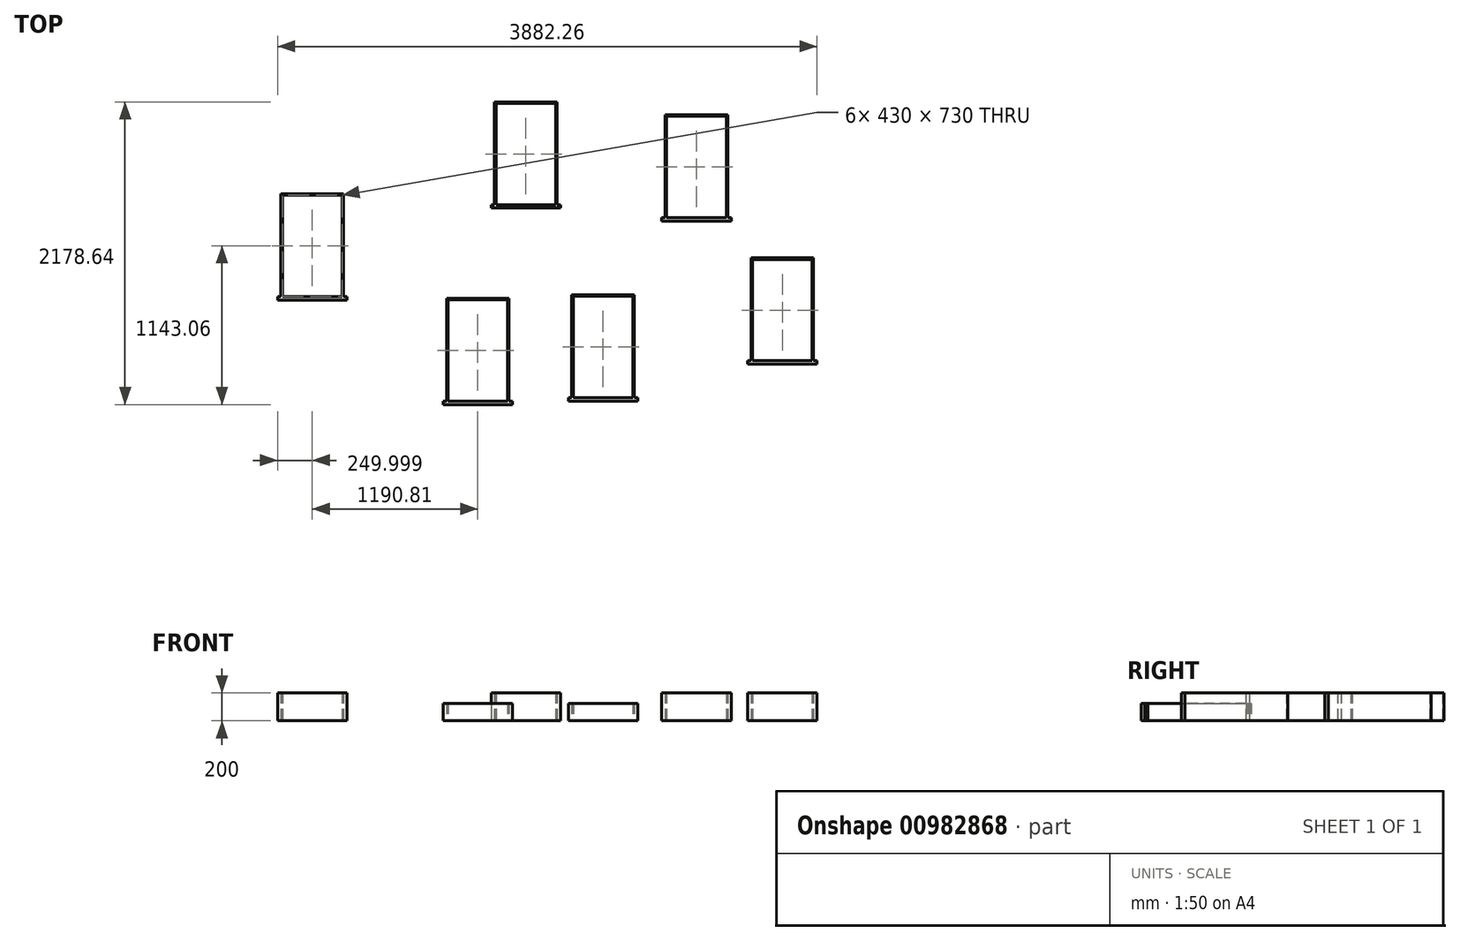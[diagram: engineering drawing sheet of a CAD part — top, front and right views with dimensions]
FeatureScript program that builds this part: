
annotation { "Feature Type Name" : "Feature", "Feature Type Description" : "" }
export const myFeature = defineFeature(function(context is Context, id is Id, definition is map)
    precondition{}
    {
        {
            var Q0;
            Q0=qCreatedBy(makeId("Top.planeOp"),FACE);
            var sketch = newSketch(context, id + "F0", { "sketchPlane" : qUnion([Q0])});
            skLineSegment(sketch, "E0.left", {"start": v(-4019.96, -780.79) * mm, "end": v(-4019.96, -1080.79) * mm});
            skLineSegment(sketch, "E1.top", {"start": v(-4044.96, -1275.79) * mm, "end": v(-4019.96, -1275.79) * mm});
            skLineSegment(sketch, "E2.left", {"start": v(-4019.96, -1275.79) * mm, "end": v(-4019.96, -1250.79) * mm});
            skLineSegment(sketch, "E3", {"start": v(-4019.96, -1250.79) * mm, "end": v(-3544.96, -1250.79) * mm});
            skLineSegment(sketch, "E4", {"start": v(-4019.96, -1275.79) * mm, "end": v(-3544.96, -1275.79) * mm});
            skLineSegment(sketch, "E5", {"start": v(-4019.96, -1250.79) * mm, "end": v(-4044.96, -1250.79) * mm});
            skLineSegment(sketch, "E6", {"start": v(-3544.96, -1275.79) * mm, "end": v(-3544.96, -1250.79) * mm});
            skLineSegment(sketch, "E7", {"start": v(-4044.96, -1275.79) * mm, "end": v(-4044.96, -1250.79) * mm});
            skLineSegment(sketch, "E8", {"start": v(-3569.96, -1271.37) * mm, "end": v(-3569.96, -510.79) * mm});
            skLineSegment(sketch, "E9", {"start": v(-4019.96, -780.79) * mm, "end": v(-4019.96, -510.79) * mm});
            skLineSegment(sketch, "E10", {"start": v(-4019.96, -1080.79) * mm, "end": v(-4019.96, -1250.79) * mm});
            skLineSegment(sketch, "E11", {"start": v(-3569.96, -510.79) * mm, "end": v(-4019.96, -510.79) * mm});
            skLineSegment(sketch, "E12", {"start": v(-4009.96, -1250.79) * mm, "end": v(-4009.96, -510.79) * mm});
            skLineSegment(sketch, "E13", {"start": v(-4019.96, -520.79) * mm, "end": v(-3569.96, -520.79) * mm});
            skLineSegment(sketch, "E14", {"start": v(-3579.96, -510.79) * mm, "end": v(-3579.96, -1250.79) * mm});
            skLineSegment(sketch, "E15", {"start": v(-3569.96, -1271.37) * mm, "end": v(-3569.96, -1275.79) * mm});
            skLineSegment(sketch, "E16.left", {"start": v(-2829.15, -1533.85) * mm, "end": v(-2829.15, -1833.85) * mm});
            skLineSegment(sketch, "E17.top", {"start": v(-2854.15, -2028.85) * mm, "end": v(-2829.15, -2028.85) * mm});
            skLineSegment(sketch, "E18.left", {"start": v(-2829.15, -2028.85) * mm, "end": v(-2829.15, -2003.85) * mm});
            skLineSegment(sketch, "E19", {"start": v(-2829.15, -2003.85) * mm, "end": v(-2354.15, -2003.85) * mm});
            skLineSegment(sketch, "E20", {"start": v(-2829.15, -2028.85) * mm, "end": v(-2354.15, -2028.85) * mm});
            skLineSegment(sketch, "E21", {"start": v(-2829.15, -2003.85) * mm, "end": v(-2854.15, -2003.85) * mm});
            skLineSegment(sketch, "E22", {"start": v(-2354.15, -2028.85) * mm, "end": v(-2354.15, -2003.85) * mm});
            skLineSegment(sketch, "E23", {"start": v(-2854.15, -2028.85) * mm, "end": v(-2854.15, -2003.85) * mm});
            skLineSegment(sketch, "E24", {"start": v(-2379.15, -2024.43) * mm, "end": v(-2379.15, -1263.85) * mm});
            skLineSegment(sketch, "E25", {"start": v(-2829.15, -1533.85) * mm, "end": v(-2829.15, -1263.85) * mm});
            skLineSegment(sketch, "E26", {"start": v(-2829.15, -1833.85) * mm, "end": v(-2829.15, -2003.85) * mm});
            skLineSegment(sketch, "E27", {"start": v(-2379.15, -1263.85) * mm, "end": v(-2829.15, -1263.85) * mm});
            skLineSegment(sketch, "E28", {"start": v(-2819.15, -2003.85) * mm, "end": v(-2819.15, -1263.85) * mm});
            skLineSegment(sketch, "E29", {"start": v(-2829.15, -1273.85) * mm, "end": v(-2379.15, -1273.85) * mm});
            skLineSegment(sketch, "E30", {"start": v(-2389.15, -1263.85) * mm, "end": v(-2389.15, -2003.85) * mm});
            skLineSegment(sketch, "E31", {"start": v(-2379.15, -2024.43) * mm, "end": v(-2379.15, -2028.85) * mm});
            skLineSegment(sketch, "E32.left", {"start": v(-1927.88, -1509.15) * mm, "end": v(-1927.88, -1809.15) * mm});
            skLineSegment(sketch, "E33.top", {"start": v(-1952.88, -2004.15) * mm, "end": v(-1927.88, -2004.15) * mm});
            skLineSegment(sketch, "E34.left", {"start": v(-1927.88, -2004.15) * mm, "end": v(-1927.88, -1979.15) * mm});
            skLineSegment(sketch, "E35", {"start": v(-1927.88, -1979.15) * mm, "end": v(-1452.88, -1979.15) * mm});
            skLineSegment(sketch, "E36", {"start": v(-1927.88, -2004.15) * mm, "end": v(-1452.88, -2004.15) * mm});
            skLineSegment(sketch, "E37", {"start": v(-1927.88, -1979.15) * mm, "end": v(-1952.88, -1979.15) * mm});
            skLineSegment(sketch, "E38", {"start": v(-1452.88, -2004.15) * mm, "end": v(-1452.88, -1979.15) * mm});
            skLineSegment(sketch, "E39", {"start": v(-1952.88, -2004.15) * mm, "end": v(-1952.88, -1979.15) * mm});
            skLineSegment(sketch, "E40", {"start": v(-1477.88, -1999.74) * mm, "end": v(-1477.88, -1239.15) * mm});
            skLineSegment(sketch, "E41", {"start": v(-1927.88, -1509.15) * mm, "end": v(-1927.88, -1239.15) * mm});
            skLineSegment(sketch, "E42", {"start": v(-1927.88, -1809.15) * mm, "end": v(-1927.88, -1979.15) * mm});
            skLineSegment(sketch, "E43", {"start": v(-1477.88, -1239.15) * mm, "end": v(-1927.88, -1239.15) * mm});
            skLineSegment(sketch, "E44", {"start": v(-1917.88, -1979.15) * mm, "end": v(-1917.88, -1239.15) * mm});
            skLineSegment(sketch, "E45", {"start": v(-1927.88, -1249.15) * mm, "end": v(-1477.88, -1249.15) * mm});
            skLineSegment(sketch, "E46", {"start": v(-1487.88, -1239.15) * mm, "end": v(-1487.88, -1979.15) * mm});
            skLineSegment(sketch, "E47", {"start": v(-1477.88, -1999.74) * mm, "end": v(-1477.88, -2004.15) * mm});
            skLineSegment(sketch, "E48.left", {"start": v(-637.7, -1243.71) * mm, "end": v(-637.7, -1543.71) * mm});
            skLineSegment(sketch, "E49.top", {"start": v(-662.7, -1738.71) * mm, "end": v(-637.7, -1738.71) * mm});
            skLineSegment(sketch, "E50.left", {"start": v(-637.7, -1738.71) * mm, "end": v(-637.7, -1713.71) * mm});
            skLineSegment(sketch, "E51", {"start": v(-637.7, -1713.71) * mm, "end": v(-162.7, -1713.71) * mm});
            skLineSegment(sketch, "E52", {"start": v(-637.7, -1738.71) * mm, "end": v(-162.7, -1738.71) * mm});
            skLineSegment(sketch, "E53", {"start": v(-637.7, -1713.71) * mm, "end": v(-662.7, -1713.71) * mm});
            skLineSegment(sketch, "E54", {"start": v(-162.7, -1738.71) * mm, "end": v(-162.7, -1713.71) * mm});
            skLineSegment(sketch, "E55", {"start": v(-662.7, -1738.71) * mm, "end": v(-662.7, -1713.71) * mm});
            skLineSegment(sketch, "E56", {"start": v(-187.7, -1734.3) * mm, "end": v(-187.7, -973.71) * mm});
            skLineSegment(sketch, "E57", {"start": v(-637.7, -1243.71) * mm, "end": v(-637.7, -973.71) * mm});
            skLineSegment(sketch, "E58", {"start": v(-637.7, -1543.71) * mm, "end": v(-637.7, -1713.71) * mm});
            skLineSegment(sketch, "E59", {"start": v(-187.7, -973.71) * mm, "end": v(-637.7, -973.71) * mm});
            skLineSegment(sketch, "E60", {"start": v(-627.7, -1713.71) * mm, "end": v(-627.7, -973.71) * mm});
            skLineSegment(sketch, "E61", {"start": v(-637.7, -983.71) * mm, "end": v(-187.7, -983.71) * mm});
            skLineSegment(sketch, "E62", {"start": v(-197.7, -973.71) * mm, "end": v(-197.7, -1713.71) * mm});
            skLineSegment(sketch, "E63", {"start": v(-187.7, -1734.3) * mm, "end": v(-187.7, -1738.71) * mm});
            skLineSegment(sketch, "E64.left", {"start": v(-2483.46, -120.2) * mm, "end": v(-2483.46, -420.2) * mm});
            skLineSegment(sketch, "E65.top", {"start": v(-2508.46, -615.2) * mm, "end": v(-2483.46, -615.2) * mm});
            skLineSegment(sketch, "E66.left", {"start": v(-2483.46, -615.2) * mm, "end": v(-2483.46, -590.2) * mm});
            skLineSegment(sketch, "E67", {"start": v(-2483.46, -590.2) * mm, "end": v(-2008.46, -590.2) * mm});
            skLineSegment(sketch, "E68", {"start": v(-2483.46, -615.2) * mm, "end": v(-2008.46, -615.2) * mm});
            skLineSegment(sketch, "E69", {"start": v(-2483.46, -590.2) * mm, "end": v(-2508.46, -590.2) * mm});
            skLineSegment(sketch, "E70", {"start": v(-2008.46, -615.2) * mm, "end": v(-2008.46, -590.2) * mm});
            skLineSegment(sketch, "E71", {"start": v(-2508.46, -615.2) * mm, "end": v(-2508.46, -590.2) * mm});
            skLineSegment(sketch, "E72", {"start": v(-2033.46, -610.8) * mm, "end": v(-2033.46, 149.8) * mm});
            skLineSegment(sketch, "E73", {"start": v(-2483.46, -120.2) * mm, "end": v(-2483.46, 149.8) * mm});
            skLineSegment(sketch, "E74", {"start": v(-2483.46, -420.2) * mm, "end": v(-2483.46, -590.2) * mm});
            skLineSegment(sketch, "E75", {"start": v(-2033.46, 149.8) * mm, "end": v(-2483.46, 149.8) * mm});
            skLineSegment(sketch, "E76", {"start": v(-2473.46, -590.2) * mm, "end": v(-2473.46, 149.8) * mm});
            skLineSegment(sketch, "E77", {"start": v(-2483.46, 139.8) * mm, "end": v(-2033.46, 139.8) * mm});
            skLineSegment(sketch, "E78", {"start": v(-2043.46, 149.8) * mm, "end": v(-2043.46, -590.2) * mm});
            skLineSegment(sketch, "E79", {"start": v(-2033.46, -610.8) * mm, "end": v(-2033.46, -615.2) * mm});
            skLineSegment(sketch, "E80.left", {"start": v(-1255.01, -212.8) * mm, "end": v(-1255.01, -512.8) * mm});
            skLineSegment(sketch, "E81.top", {"start": v(-1280.01, -707.8) * mm, "end": v(-1255.01, -707.8) * mm});
            skLineSegment(sketch, "E82.left", {"start": v(-1255.01, -707.8) * mm, "end": v(-1255.01, -682.8) * mm});
            skLineSegment(sketch, "E83", {"start": v(-1255.01, -682.8) * mm, "end": v(-780.01, -682.8) * mm});
            skLineSegment(sketch, "E84", {"start": v(-1255.01, -707.8) * mm, "end": v(-780.01, -707.8) * mm});
            skLineSegment(sketch, "E85", {"start": v(-1255.01, -682.8) * mm, "end": v(-1280.01, -682.8) * mm});
            skLineSegment(sketch, "E86", {"start": v(-780.01, -707.8) * mm, "end": v(-780.01, -682.8) * mm});
            skLineSegment(sketch, "E87", {"start": v(-1280.01, -707.8) * mm, "end": v(-1280.01, -682.8) * mm});
            skLineSegment(sketch, "E88", {"start": v(-805.01, -703.39) * mm, "end": v(-805.01, 57.2) * mm});
            skLineSegment(sketch, "E89", {"start": v(-1255.01, -212.8) * mm, "end": v(-1255.01, 57.2) * mm});
            skLineSegment(sketch, "E90", {"start": v(-1255.01, -512.8) * mm, "end": v(-1255.01, -682.8) * mm});
            skLineSegment(sketch, "E91", {"start": v(-805.01, 57.2) * mm, "end": v(-1255.01, 57.2) * mm});
            skLineSegment(sketch, "E92", {"start": v(-1245.01, -682.8) * mm, "end": v(-1245.01, 57.2) * mm});
            skLineSegment(sketch, "E93", {"start": v(-1255.01, 47.2) * mm, "end": v(-805.01, 47.2) * mm});
            skLineSegment(sketch, "E94", {"start": v(-815.01, 57.2) * mm, "end": v(-815.01, -682.8) * mm});
            skLineSegment(sketch, "E95", {"start": v(-805.01, -703.39) * mm, "end": v(-805.01, -707.8) * mm});
            skSolve(sketch);
        }
        {
            var Q0;
            {var subQ5=sQuery(id+"F0.wireOp",EDGE,"E0.left");Q0=makeQuery(id+"F0.imprint","IMPRINT",FACE,{"disambiguationData":[TD([[makeQuery(id+"F0.imprint","IMPRINT",EDGE,{"derivedFrom":subQ5}),1.0]])]});}
            var Q1;
            {var subQ0=sQuery(id+"F0.wireOp",EDGE,"E12");var subQ1=sQuery(id+"F0.wireOp",EDGE,"E11");var subQ2=makeQuery(id+"F0.imprint","INTERSECT",VERTEX,{"derivedFrom":[subQ1,subQ0]});Q1=makeQuery(id+"F0.imprint","IMPRINT",FACE,{"disambiguationData":[TD([[makeQuery(id+"F0.imprint","IMPRINT",EDGE,{"disambiguationData":[TD([[subQ2,1.0]])],"derivedFrom":subQ1}),1.0]])]});}
            var Q2;
            {var subQ0=sQuery(id+"F0.wireOp",EDGE,"E11");var subQ1=sQuery(id+"F0.wireOp",EDGE,"E9");var subQ2=makeQuery(id+"F0.imprint","INTERSECT",VERTEX,{"derivedFrom":[subQ1,subQ0]});Q2=makeQuery(id+"F0.imprint","IMPRINT",FACE,{"disambiguationData":[TD([[makeQuery(id+"F0.imprint","IMPRINT",EDGE,{"disambiguationData":[TD([[subQ2,1.0]])],"derivedFrom":subQ1}),-1.0]])]});}
            var Q3;
            {var subQ0=sQuery(id+"F0.wireOp",EDGE,"E11");var subQ1=sQuery(id+"F0.wireOp",EDGE,"E8");var subQ2=makeQuery(id+"F0.imprint","INTERSECT",VERTEX,{"derivedFrom":[subQ1,subQ0]});Q3=makeQuery(id+"F0.imprint","IMPRINT",FACE,{"disambiguationData":[TD([[makeQuery(id+"F0.imprint","IMPRINT",EDGE,{"disambiguationData":[TD([[subQ2,1.0]])],"derivedFrom":subQ1}),1.0]])]});}
            var Q4;
            {var subQ0=sQuery(id+"F0.wireOp",EDGE,"E14");var subQ1=sQuery(id+"F0.wireOp",EDGE,"E3");var subQ2=makeQuery(id+"F0.imprint","INTERSECT",VERTEX,{"derivedFrom":[subQ1,subQ0]});Q4=makeQuery(id+"F0.imprint","IMPRINT",FACE,{"disambiguationData":[TD([[makeQuery(id+"F0.imprint","IMPRINT",EDGE,{"disambiguationData":[TD([[subQ2,-1.0]])],"derivedFrom":subQ1}),1.0]])]});}
            var Q5;
            {var subQ4=sQuery(id+"F0.wireOp",EDGE,"E6");Q5=makeQuery(id+"F0.imprint","IMPRINT",FACE,{"disambiguationData":[TD([[makeQuery(id+"F0.imprint","IMPRINT",EDGE,{"derivedFrom":subQ4}),1.0]])]});}
            var Q6;
            {var subQ5=sQuery(id+"F0.wireOp",EDGE,"E2.left");Q6=makeQuery(id+"F0.imprint","IMPRINT",FACE,{"disambiguationData":[TD([[makeQuery(id+"F0.imprint","IMPRINT",EDGE,{"derivedFrom":subQ5}),-1.0]])]});}
            var Q7;
            Q7=makeQuery(id+"F0.imprint","IMPRINT",FACE,{"disambiguationData":[TD([[makeQuery(id+"F0.imprint","IMPRINT",EDGE,{"derivedFrom":sQuery(id+"F0.wireOp",EDGE,"E1.top")}),1.0]])]});
            var Q8;
            {var subQ5=sQuery(id+"F0.wireOp",EDGE,"E64.left");Q8=makeQuery(id+"F0.imprint","IMPRINT",FACE,{"disambiguationData":[TD([[makeQuery(id+"F0.imprint","IMPRINT",EDGE,{"derivedFrom":subQ5}),1.0]])]});}
            var Q9;
            {var subQ0=sQuery(id+"F0.wireOp",EDGE,"E75");var subQ1=sQuery(id+"F0.wireOp",EDGE,"E73");var subQ2=makeQuery(id+"F0.imprint","INTERSECT",VERTEX,{"derivedFrom":[subQ1,subQ0]});Q9=makeQuery(id+"F0.imprint","IMPRINT",FACE,{"disambiguationData":[TD([[makeQuery(id+"F0.imprint","IMPRINT",EDGE,{"disambiguationData":[TD([[subQ2,1.0]])],"derivedFrom":subQ1}),-1.0]])]});}
            var Q10;
            {var subQ0=sQuery(id+"F0.wireOp",EDGE,"E76");var subQ1=sQuery(id+"F0.wireOp",EDGE,"E75");var subQ2=makeQuery(id+"F0.imprint","INTERSECT",VERTEX,{"derivedFrom":[subQ1,subQ0]});Q10=makeQuery(id+"F0.imprint","IMPRINT",FACE,{"disambiguationData":[TD([[makeQuery(id+"F0.imprint","IMPRINT",EDGE,{"disambiguationData":[TD([[subQ2,1.0]])],"derivedFrom":subQ1}),1.0]])]});}
            var Q11;
            {var subQ0=sQuery(id+"F0.wireOp",EDGE,"E78");var subQ1=sQuery(id+"F0.wireOp",EDGE,"E67");var subQ2=makeQuery(id+"F0.imprint","INTERSECT",VERTEX,{"derivedFrom":[subQ1,subQ0]});Q11=makeQuery(id+"F0.imprint","IMPRINT",FACE,{"disambiguationData":[TD([[makeQuery(id+"F0.imprint","IMPRINT",EDGE,{"disambiguationData":[TD([[subQ2,-1.0]])],"derivedFrom":subQ1}),1.0]])]});}
            var Q12;
            {var subQ0=sQuery(id+"F0.wireOp",EDGE,"E75");var subQ1=sQuery(id+"F0.wireOp",EDGE,"E72");var subQ2=makeQuery(id+"F0.imprint","INTERSECT",VERTEX,{"derivedFrom":[subQ1,subQ0]});Q12=makeQuery(id+"F0.imprint","IMPRINT",FACE,{"disambiguationData":[TD([[makeQuery(id+"F0.imprint","IMPRINT",EDGE,{"disambiguationData":[TD([[subQ2,1.0]])],"derivedFrom":subQ1}),1.0]])]});}
            var Q13;
            {var subQ5=sQuery(id+"F0.wireOp",EDGE,"E66.left");Q13=makeQuery(id+"F0.imprint","IMPRINT",FACE,{"disambiguationData":[TD([[makeQuery(id+"F0.imprint","IMPRINT",EDGE,{"derivedFrom":subQ5}),-1.0]])]});}
            var Q14;
            {var subQ4=sQuery(id+"F0.wireOp",EDGE,"E70");Q14=makeQuery(id+"F0.imprint","IMPRINT",FACE,{"disambiguationData":[TD([[makeQuery(id+"F0.imprint","IMPRINT",EDGE,{"derivedFrom":subQ4}),1.0]])]});}
            var Q15;
            Q15=makeQuery(id+"F0.imprint","IMPRINT",FACE,{"disambiguationData":[TD([[makeQuery(id+"F0.imprint","IMPRINT",EDGE,{"derivedFrom":sQuery(id+"F0.wireOp",EDGE,"E65.top")}),1.0]])]});
            var Q16;
            Q16=makeQuery(id+"F0.imprint","IMPRINT",FACE,{"disambiguationData":[TD([[makeQuery(id+"F0.imprint","IMPRINT",EDGE,{"derivedFrom":sQuery(id+"F0.wireOp",EDGE,"E81.top")}),1.0]])]});
            var Q17;
            {var subQ5=sQuery(id+"F0.wireOp",EDGE,"E82.left");Q17=makeQuery(id+"F0.imprint","IMPRINT",FACE,{"disambiguationData":[TD([[makeQuery(id+"F0.imprint","IMPRINT",EDGE,{"derivedFrom":subQ5}),-1.0]])]});}
            var Q18;
            {var subQ4=sQuery(id+"F0.wireOp",EDGE,"E86");Q18=makeQuery(id+"F0.imprint","IMPRINT",FACE,{"disambiguationData":[TD([[makeQuery(id+"F0.imprint","IMPRINT",EDGE,{"derivedFrom":subQ4}),1.0]])]});}
            var Q19;
            {var subQ0=sQuery(id+"F0.wireOp",EDGE,"E94");var subQ1=sQuery(id+"F0.wireOp",EDGE,"E83");var subQ2=makeQuery(id+"F0.imprint","INTERSECT",VERTEX,{"derivedFrom":[subQ1,subQ0]});Q19=makeQuery(id+"F0.imprint","IMPRINT",FACE,{"disambiguationData":[TD([[makeQuery(id+"F0.imprint","IMPRINT",EDGE,{"disambiguationData":[TD([[subQ2,-1.0]])],"derivedFrom":subQ1}),1.0]])]});}
            var Q20;
            {var subQ5=sQuery(id+"F0.wireOp",EDGE,"E80.left");Q20=makeQuery(id+"F0.imprint","IMPRINT",FACE,{"disambiguationData":[TD([[makeQuery(id+"F0.imprint","IMPRINT",EDGE,{"derivedFrom":subQ5}),1.0]])]});}
            var Q21;
            {var subQ0=sQuery(id+"F0.wireOp",EDGE,"E91");var subQ1=sQuery(id+"F0.wireOp",EDGE,"E89");var subQ2=makeQuery(id+"F0.imprint","INTERSECT",VERTEX,{"derivedFrom":[subQ1,subQ0]});Q21=makeQuery(id+"F0.imprint","IMPRINT",FACE,{"disambiguationData":[TD([[makeQuery(id+"F0.imprint","IMPRINT",EDGE,{"disambiguationData":[TD([[subQ2,1.0]])],"derivedFrom":subQ1}),-1.0]])]});}
            var Q22;
            {var subQ0=sQuery(id+"F0.wireOp",EDGE,"E92");var subQ1=sQuery(id+"F0.wireOp",EDGE,"E91");var subQ2=makeQuery(id+"F0.imprint","INTERSECT",VERTEX,{"derivedFrom":[subQ1,subQ0]});Q22=makeQuery(id+"F0.imprint","IMPRINT",FACE,{"disambiguationData":[TD([[makeQuery(id+"F0.imprint","IMPRINT",EDGE,{"disambiguationData":[TD([[subQ2,1.0]])],"derivedFrom":subQ1}),1.0]])]});}
            var Q23;
            {var subQ0=sQuery(id+"F0.wireOp",EDGE,"E91");var subQ1=sQuery(id+"F0.wireOp",EDGE,"E88");var subQ2=makeQuery(id+"F0.imprint","INTERSECT",VERTEX,{"derivedFrom":[subQ1,subQ0]});Q23=makeQuery(id+"F0.imprint","IMPRINT",FACE,{"disambiguationData":[TD([[makeQuery(id+"F0.imprint","IMPRINT",EDGE,{"disambiguationData":[TD([[subQ2,1.0]])],"derivedFrom":subQ1}),1.0]])]});}
            var Q24;
            {var subQ0=sQuery(id+"F0.wireOp",EDGE,"E59");var subQ1=sQuery(id+"F0.wireOp",EDGE,"E57");var subQ2=makeQuery(id+"F0.imprint","INTERSECT",VERTEX,{"derivedFrom":[subQ1,subQ0]});Q24=makeQuery(id+"F0.imprint","IMPRINT",FACE,{"disambiguationData":[TD([[makeQuery(id+"F0.imprint","IMPRINT",EDGE,{"disambiguationData":[TD([[subQ2,1.0]])],"derivedFrom":subQ1}),-1.0]])]});}
            var Q25;
            {var subQ0=sQuery(id+"F0.wireOp",EDGE,"E60");var subQ1=sQuery(id+"F0.wireOp",EDGE,"E59");var subQ2=makeQuery(id+"F0.imprint","INTERSECT",VERTEX,{"derivedFrom":[subQ1,subQ0]});Q25=makeQuery(id+"F0.imprint","IMPRINT",FACE,{"disambiguationData":[TD([[makeQuery(id+"F0.imprint","IMPRINT",EDGE,{"disambiguationData":[TD([[subQ2,1.0]])],"derivedFrom":subQ1}),1.0]])]});}
            var Q26;
            {var subQ0=sQuery(id+"F0.wireOp",EDGE,"E59");var subQ1=sQuery(id+"F0.wireOp",EDGE,"E56");var subQ2=makeQuery(id+"F0.imprint","INTERSECT",VERTEX,{"derivedFrom":[subQ1,subQ0]});Q26=makeQuery(id+"F0.imprint","IMPRINT",FACE,{"disambiguationData":[TD([[makeQuery(id+"F0.imprint","IMPRINT",EDGE,{"disambiguationData":[TD([[subQ2,1.0]])],"derivedFrom":subQ1}),1.0]])]});}
            var Q27;
            {var subQ0=sQuery(id+"F0.wireOp",EDGE,"E62");var subQ1=sQuery(id+"F0.wireOp",EDGE,"E51");var subQ2=makeQuery(id+"F0.imprint","INTERSECT",VERTEX,{"derivedFrom":[subQ1,subQ0]});Q27=makeQuery(id+"F0.imprint","IMPRINT",FACE,{"disambiguationData":[TD([[makeQuery(id+"F0.imprint","IMPRINT",EDGE,{"disambiguationData":[TD([[subQ2,-1.0]])],"derivedFrom":subQ1}),1.0]])]});}
            var Q28;
            {var subQ5=sQuery(id+"F0.wireOp",EDGE,"E48.left");Q28=makeQuery(id+"F0.imprint","IMPRINT",FACE,{"disambiguationData":[TD([[makeQuery(id+"F0.imprint","IMPRINT",EDGE,{"derivedFrom":subQ5}),1.0]])]});}
            var Q29;
            Q29=makeQuery(id+"F0.imprint","IMPRINT",FACE,{"disambiguationData":[TD([[makeQuery(id+"F0.imprint","IMPRINT",EDGE,{"derivedFrom":sQuery(id+"F0.wireOp",EDGE,"E49.top")}),1.0]])]});
            var Q30;
            {var subQ5=sQuery(id+"F0.wireOp",EDGE,"E50.left");Q30=makeQuery(id+"F0.imprint","IMPRINT",FACE,{"disambiguationData":[TD([[makeQuery(id+"F0.imprint","IMPRINT",EDGE,{"derivedFrom":subQ5}),-1.0]])]});}
            var Q31;
            {var subQ4=sQuery(id+"F0.wireOp",EDGE,"E54");Q31=makeQuery(id+"F0.imprint","IMPRINT",FACE,{"disambiguationData":[TD([[makeQuery(id+"F0.imprint","IMPRINT",EDGE,{"derivedFrom":subQ4}),1.0]])]});}
            extrude(context, id + "F1", {"entities" : qUnion([Q0, Q1, Q2, Q3, Q4, Q5, Q6, Q7, Q8, Q9, Q10, Q11, Q12, Q13, Q14, Q15, Q16, Q17, Q18, Q19, Q20, Q21, Q22, Q23, Q24, Q25, Q26, Q27, Q28, Q29, Q30, Q31]), "depth" : 200 * mm, "offsetDistance" : 25 * mm});
        }
        {
            var Q0;
            Q0=makeQuery(id+"F0.imprint","IMPRINT",FACE,{"disambiguationData":[TD([[makeQuery(id+"F0.imprint","IMPRINT",EDGE,{"derivedFrom":sQuery(id+"F0.wireOp",EDGE,"E17.top")}),1.0]])]});
            var Q1;
            {var subQ5=sQuery(id+"F0.wireOp",EDGE,"E18.left");Q1=makeQuery(id+"F0.imprint","IMPRINT",FACE,{"disambiguationData":[TD([[makeQuery(id+"F0.imprint","IMPRINT",EDGE,{"derivedFrom":subQ5}),-1.0]])]});}
            var Q2;
            {var subQ4=sQuery(id+"F0.wireOp",EDGE,"E22");Q2=makeQuery(id+"F0.imprint","IMPRINT",FACE,{"disambiguationData":[TD([[makeQuery(id+"F0.imprint","IMPRINT",EDGE,{"derivedFrom":subQ4}),1.0]])]});}
            var Q3;
            {var subQ0=sQuery(id+"F0.wireOp",EDGE,"E30");var subQ1=sQuery(id+"F0.wireOp",EDGE,"E19");var subQ2=makeQuery(id+"F0.imprint","INTERSECT",VERTEX,{"derivedFrom":[subQ1,subQ0]});Q3=makeQuery(id+"F0.imprint","IMPRINT",FACE,{"disambiguationData":[TD([[makeQuery(id+"F0.imprint","IMPRINT",EDGE,{"disambiguationData":[TD([[subQ2,-1.0]])],"derivedFrom":subQ1}),1.0]])]});}
            var Q4;
            {var subQ0=sQuery(id+"F0.wireOp",EDGE,"E27");var subQ1=sQuery(id+"F0.wireOp",EDGE,"E24");var subQ2=makeQuery(id+"F0.imprint","INTERSECT",VERTEX,{"derivedFrom":[subQ1,subQ0]});Q4=makeQuery(id+"F0.imprint","IMPRINT",FACE,{"disambiguationData":[TD([[makeQuery(id+"F0.imprint","IMPRINT",EDGE,{"disambiguationData":[TD([[subQ2,1.0]])],"derivedFrom":subQ1}),1.0]])]});}
            var Q5;
            {var subQ0=sQuery(id+"F0.wireOp",EDGE,"E28");var subQ1=sQuery(id+"F0.wireOp",EDGE,"E27");var subQ2=makeQuery(id+"F0.imprint","INTERSECT",VERTEX,{"derivedFrom":[subQ1,subQ0]});Q5=makeQuery(id+"F0.imprint","IMPRINT",FACE,{"disambiguationData":[TD([[makeQuery(id+"F0.imprint","IMPRINT",EDGE,{"disambiguationData":[TD([[subQ2,1.0]])],"derivedFrom":subQ1}),1.0]])]});}
            var Q6;
            {var subQ5=sQuery(id+"F0.wireOp",EDGE,"E16.left");Q6=makeQuery(id+"F0.imprint","IMPRINT",FACE,{"disambiguationData":[TD([[makeQuery(id+"F0.imprint","IMPRINT",EDGE,{"derivedFrom":subQ5}),1.0]])]});}
            var Q7;
            {var subQ0=sQuery(id+"F0.wireOp",EDGE,"E27");var subQ1=sQuery(id+"F0.wireOp",EDGE,"E25");var subQ2=makeQuery(id+"F0.imprint","INTERSECT",VERTEX,{"derivedFrom":[subQ1,subQ0]});Q7=makeQuery(id+"F0.imprint","IMPRINT",FACE,{"disambiguationData":[TD([[makeQuery(id+"F0.imprint","IMPRINT",EDGE,{"disambiguationData":[TD([[subQ2,1.0]])],"derivedFrom":subQ1}),-1.0]])]});}
            var Q8;
            {var subQ0=sQuery(id+"F0.wireOp",EDGE,"E44");var subQ1=sQuery(id+"F0.wireOp",EDGE,"E43");var subQ2=makeQuery(id+"F0.imprint","INTERSECT",VERTEX,{"derivedFrom":[subQ1,subQ0]});Q8=makeQuery(id+"F0.imprint","IMPRINT",FACE,{"disambiguationData":[TD([[makeQuery(id+"F0.imprint","IMPRINT",EDGE,{"disambiguationData":[TD([[subQ2,1.0]])],"derivedFrom":subQ1}),1.0]])]});}
            var Q9;
            {var subQ0=sQuery(id+"F0.wireOp",EDGE,"E43");var subQ1=sQuery(id+"F0.wireOp",EDGE,"E41");var subQ2=makeQuery(id+"F0.imprint","INTERSECT",VERTEX,{"derivedFrom":[subQ1,subQ0]});Q9=makeQuery(id+"F0.imprint","IMPRINT",FACE,{"disambiguationData":[TD([[makeQuery(id+"F0.imprint","IMPRINT",EDGE,{"disambiguationData":[TD([[subQ2,1.0]])],"derivedFrom":subQ1}),-1.0]])]});}
            var Q10;
            {var subQ5=sQuery(id+"F0.wireOp",EDGE,"E32.left");Q10=makeQuery(id+"F0.imprint","IMPRINT",FACE,{"disambiguationData":[TD([[makeQuery(id+"F0.imprint","IMPRINT",EDGE,{"derivedFrom":subQ5}),1.0]])]});}
            var Q11;
            Q11=makeQuery(id+"F0.imprint","IMPRINT",FACE,{"disambiguationData":[TD([[makeQuery(id+"F0.imprint","IMPRINT",EDGE,{"derivedFrom":sQuery(id+"F0.wireOp",EDGE,"E33.top")}),1.0]])]});
            var Q12;
            {var subQ5=sQuery(id+"F0.wireOp",EDGE,"E34.left");Q12=makeQuery(id+"F0.imprint","IMPRINT",FACE,{"disambiguationData":[TD([[makeQuery(id+"F0.imprint","IMPRINT",EDGE,{"derivedFrom":subQ5}),-1.0]])]});}
            var Q13;
            {var subQ4=sQuery(id+"F0.wireOp",EDGE,"E38");Q13=makeQuery(id+"F0.imprint","IMPRINT",FACE,{"disambiguationData":[TD([[makeQuery(id+"F0.imprint","IMPRINT",EDGE,{"derivedFrom":subQ4}),1.0]])]});}
            var Q14;
            {var subQ0=sQuery(id+"F0.wireOp",EDGE,"E46");var subQ1=sQuery(id+"F0.wireOp",EDGE,"E35");var subQ2=makeQuery(id+"F0.imprint","INTERSECT",VERTEX,{"derivedFrom":[subQ1,subQ0]});Q14=makeQuery(id+"F0.imprint","IMPRINT",FACE,{"disambiguationData":[TD([[makeQuery(id+"F0.imprint","IMPRINT",EDGE,{"disambiguationData":[TD([[subQ2,-1.0]])],"derivedFrom":subQ1}),1.0]])]});}
            var Q15;
            {var subQ0=sQuery(id+"F0.wireOp",EDGE,"E43");var subQ1=sQuery(id+"F0.wireOp",EDGE,"E40");var subQ2=makeQuery(id+"F0.imprint","INTERSECT",VERTEX,{"derivedFrom":[subQ1,subQ0]});Q15=makeQuery(id+"F0.imprint","IMPRINT",FACE,{"disambiguationData":[TD([[makeQuery(id+"F0.imprint","IMPRINT",EDGE,{"disambiguationData":[TD([[subQ2,1.0]])],"derivedFrom":subQ1}),1.0]])]});}
            extrude(context, id + "F2", {"entities" : qUnion([Q0, Q1, Q2, Q3, Q4, Q5, Q6, Q7, Q8, Q9, Q10, Q11, Q12, Q13, Q14, Q15]), "depth" : 125 * mm, "offsetDistance" : 25 * mm});
        }
        {
            var Q0;
            {var subQ0=sQuery(id+"F0.wireOp",EDGE,"E28");var subQ1=sQuery(id+"F0.wireOp",EDGE,"E19");var subQ2=makeQuery(id+"F0.imprint","INTERSECT",VERTEX,{"derivedFrom":[subQ1,subQ0]});Q0=makeQuery(id+"F0.imprint","IMPRINT",FACE,{"disambiguationData":[TD([[makeQuery(id+"F0.imprint","IMPRINT",EDGE,{"disambiguationData":[TD([[subQ2,-1.0]])],"derivedFrom":subQ1}),1.0]])]});}
            var Q1;
            {var subQ0=sQuery(id+"F0.wireOp",EDGE,"E44");var subQ1=sQuery(id+"F0.wireOp",EDGE,"E35");var subQ2=makeQuery(id+"F0.imprint","INTERSECT",VERTEX,{"derivedFrom":[subQ1,subQ0]});Q1=makeQuery(id+"F0.imprint","IMPRINT",FACE,{"disambiguationData":[TD([[makeQuery(id+"F0.imprint","IMPRINT",EDGE,{"disambiguationData":[TD([[subQ2,-1.0]])],"derivedFrom":subQ1}),1.0]])]});}
            var Q2;
            {var subQ0=sQuery(id+"F0.wireOp",EDGE,"E60");var subQ1=sQuery(id+"F0.wireOp",EDGE,"E51");var subQ2=makeQuery(id+"F0.imprint","INTERSECT",VERTEX,{"derivedFrom":[subQ1,subQ0]});Q2=makeQuery(id+"F0.imprint","IMPRINT",FACE,{"disambiguationData":[TD([[makeQuery(id+"F0.imprint","IMPRINT",EDGE,{"disambiguationData":[TD([[subQ2,-1.0]])],"derivedFrom":subQ1}),1.0]])]});}
            var Q3;
            {var subQ0=sQuery(id+"F0.wireOp",EDGE,"E92");var subQ1=sQuery(id+"F0.wireOp",EDGE,"E83");var subQ2=makeQuery(id+"F0.imprint","INTERSECT",VERTEX,{"derivedFrom":[subQ1,subQ0]});Q3=makeQuery(id+"F0.imprint","IMPRINT",FACE,{"disambiguationData":[TD([[makeQuery(id+"F0.imprint","IMPRINT",EDGE,{"disambiguationData":[TD([[subQ2,-1.0]])],"derivedFrom":subQ1}),1.0]])]});}
            var Q4;
            {var subQ0=sQuery(id+"F0.wireOp",EDGE,"E76");var subQ1=sQuery(id+"F0.wireOp",EDGE,"E67");var subQ2=makeQuery(id+"F0.imprint","INTERSECT",VERTEX,{"derivedFrom":[subQ1,subQ0]});Q4=makeQuery(id+"F0.imprint","IMPRINT",FACE,{"disambiguationData":[TD([[makeQuery(id+"F0.imprint","IMPRINT",EDGE,{"disambiguationData":[TD([[subQ2,-1.0]])],"derivedFrom":subQ1}),1.0]])]});}
            var Q5;
            {var subQ0=sQuery(id+"F0.wireOp",EDGE,"E12");var subQ1=sQuery(id+"F0.wireOp",EDGE,"E3");var subQ2=makeQuery(id+"F0.imprint","INTERSECT",VERTEX,{"derivedFrom":[subQ1,subQ0]});Q5=makeQuery(id+"F0.imprint","IMPRINT",FACE,{"disambiguationData":[TD([[makeQuery(id+"F0.imprint","IMPRINT",EDGE,{"disambiguationData":[TD([[subQ2,-1.0]])],"derivedFrom":subQ1}),1.0]])]});}
            extrude(context, id + "F3", {"entities" : qUnion([Q0, Q1, Q2, Q3, Q4, Q5]), "depth" : 5 * mm, "offsetDistance" : 25 * mm});
        }
    });
